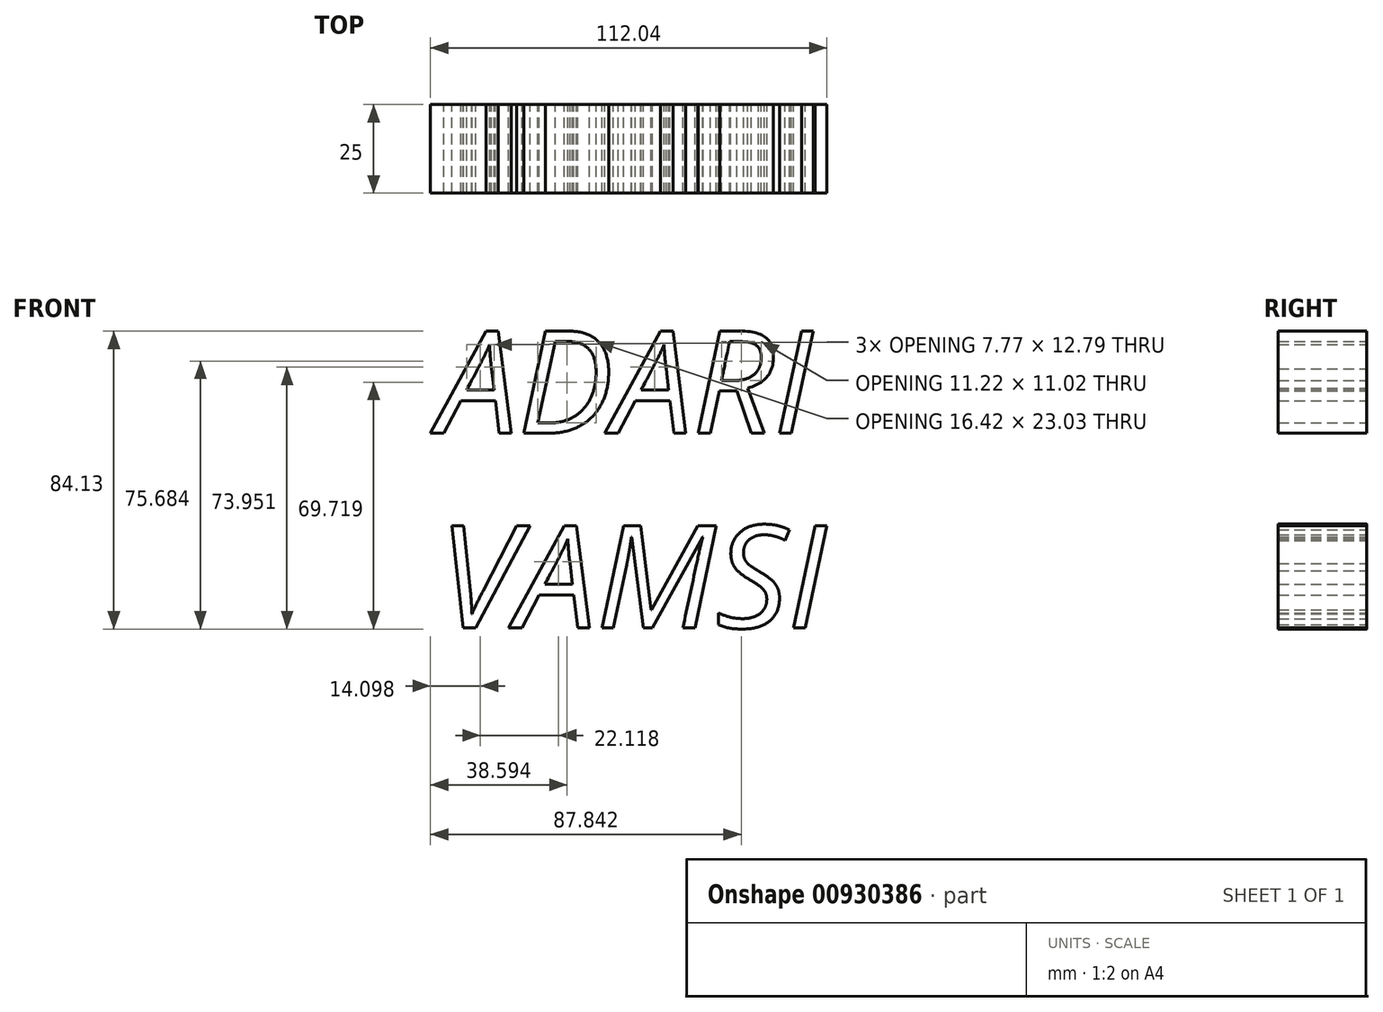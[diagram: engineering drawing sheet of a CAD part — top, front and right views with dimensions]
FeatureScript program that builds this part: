
annotation { "Feature Type Name" : "Feature", "Feature Type Description" : "" }
export const myFeature = defineFeature(function(context is Context, id is Id, definition is map)
    precondition{}
    {
        {
            var Q0;
            Q0=qCreatedBy(makeId("Front.planeOp"),FACE);
            var sketch = newSketch(context, id + "F0", { "sketchPlane" : qUnion([Q0])});
            skText(sketch, "E0", { "text": "ADARI\nVAMSI", "fontName": "OpenSans-Italic.ttf"});
            const initialGuessF0  = {"E0": [-0.05733, -0.02907, 1, 0, 0.02907]};
            skSetInitialGuess(sketch, initialGuessF0);
            skSolve(sketch);
        }
        {
            var Q0;
            Q0 = qSketchRegion(id + "F0", true);
            extrude(context, id + "F1", {"entities" : qUnion([Q0]), "depth" : 25 * mm, "offsetDistance" : 25 * mm});
        }
    });
